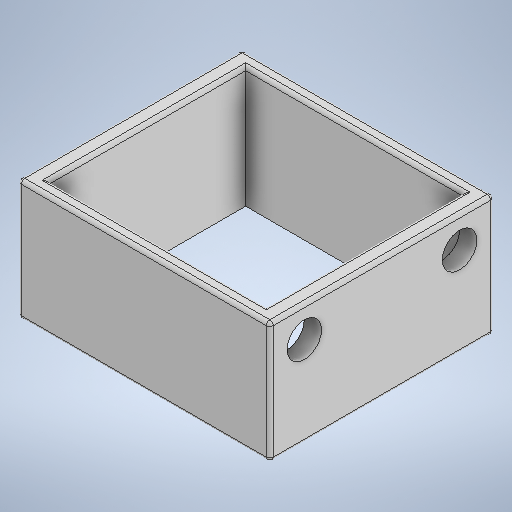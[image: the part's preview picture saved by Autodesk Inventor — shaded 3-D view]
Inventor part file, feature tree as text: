
AUTODESK INVENTOR PART (.ipt)
format: ipt  version: 2025 (Build 290162000, 162)  size: 252,928 bytes
history: native  units: in
note: dims shown in document units (in); Inventor stores cm internally (conversion verified against a paired STEP export)
features: extrude x3, sketch x3, fillet x2
ambient origin geometry x8: Origin, YZ Plane, XZ Plane, XY Plane, X Axis, Y Axis, Z Axis, Center Point
bodies: Solid1 (feature_tree)
feature tree (8):
  extrude  "Extrusion1"  Depth=13.7795in
  fillet  "Fillet1"  Radius=25.5906in
  extrude  "Extrusion2"  Depth=24.8031in
  fillet  "Fillet2"  Radius=22.4409in
  extrude  "Extrusion3"  Depth=1.5748in
  sketch  "Sketch1"  dims[d0=28.7402in d1=13.7795in d2=25.5906in d3=0.0in]
  sketch  "Sketch2"  dims[d4=0.3937in d5=24.8031in d6=22.4409in]
  sketch  "Sketch3"  dims[d7=1.1811in d8=1.5748in d9=13.7795in d10=0.0in d11=0.3937in d12=3.5433in d13=3.5433in d14=3.937in d15=3.937in d16=9.8425in d17=9.8425in d18=13.7795in d19=0.0in]
